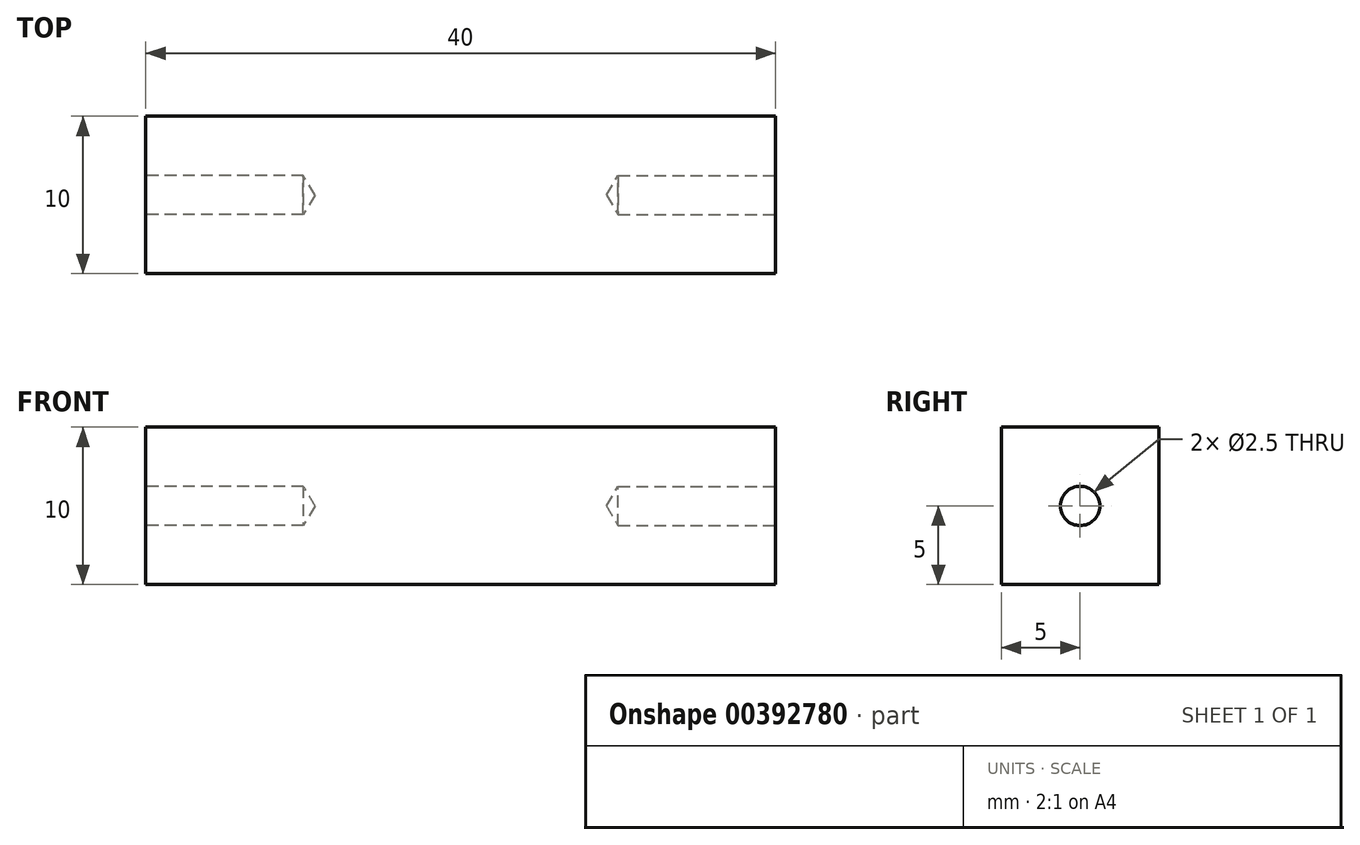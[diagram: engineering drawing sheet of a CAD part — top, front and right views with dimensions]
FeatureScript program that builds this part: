
annotation { "Feature Type Name" : "Feature", "Feature Type Description" : "" }
export const myFeature = defineFeature(function(context is Context, id is Id, definition is map)
    precondition{}
    {
        {
            var Q0;
            Q0=qCreatedBy(makeId("Right.planeOp"),FACE);
            var sketch = newSketch(context, id + "F0", { "sketchPlane" : qUnion([Q0])});
            skLineSegment(sketch, "E0.bottom", {"start": v(0, 0) * mm, "end": v(-10, 0) * mm});
            skLineSegment(sketch, "E0.top", {"start": v(0, 10) * mm, "end": v(-10, 10) * mm});
            skLineSegment(sketch, "E0.left", {"start": v(0, 0) * mm, "end": v(0, 10) * mm});
            skLineSegment(sketch, "E0.right", {"start": v(-10, 0) * mm, "end": v(-10, 10) * mm});
            skSolve(sketch);
        }
        {
            var Q0;
            Q0=makeQuery(id+"F0.imprint","IMPRINT",FACE,{"disambiguationData":[TD([[makeQuery(id+"F0.imprint","IMPRINT",EDGE,{"derivedFrom":sQuery(id+"F0.wireOp",EDGE,"E0.bottom")}),-1.0]])]});
            extrude(context, id + "F1", {"entities" : qUnion([Q0]), "depth" : 40 * mm});
        }
        {
            var Q0;
            Q0=makeQuery(id+"F1.opExtrude","CAP_FACE",FACE,{"disambiguationData":[OSD([sQuery(id+"F0.wireOp",EDGE,"E0.bottom"),sQuery(id+"F0.wireOp",EDGE,"E0.top"),sQuery(id+"F0.wireOp",EDGE,"E0.left"),sQuery(id+"F0.wireOp",EDGE,"E0.right")])],"isStart":false});
            var sketch = newSketch(context, id + "F2", { "sketchPlane" : qUnion([Q0])});
            skPoint(sketch, "E1.oppositeSnap0", {"position": v(0, 5) * mm});
            skLineSegment(sketch, "E1.bottom", {"start": v(0, 10) * mm, "end": v(-5, 10) * mm});
            skLineSegment(sketch, "E1.top", {"start": v(0, 5) * mm, "end": v(-5, 5) * mm});
            skLineSegment(sketch, "E1.left", {"start": v(0, 10) * mm, "end": v(0, 5) * mm});
            skLineSegment(sketch, "E1.right", {"start": v(-5, 10) * mm, "end": v(-5, 5) * mm});
            skSolve(sketch);
        }
        {
            var Q0;
            Q0=sQuery(id+"F2.wireOp",VERTEX,"E1.top.end");
            var Q1;
            Q1=makeQuery(id+"F1.opExtrude","SWEPT_BODY",BODY,{"disambiguationData":[OSD([sQuery(id+"F0.wireOp",EDGE,"E0.bottom"),sQuery(id+"F0.wireOp",EDGE,"E0.top"),sQuery(id+"F0.wireOp",EDGE,"E0.left"),sQuery(id+"F0.wireOp",EDGE,"E0.right")])]});
            hole(context, id + "F3", {"style" : HoleStyle.SIMPLE, "endStyle" : HoleEndStyle.BLIND, "holeDiameter" : 2.5 * mm, "holeDepth" : 10 * mm, "isTappedThrough" : true, "tappedDepth" : 12 * mm, "tapClearance" : 3, "locations" : qUnion([Q0]), "scope" : qUnion([Q1])});
        }
        {
            var Q0;
            Q0=makeQuery(id+"F1.opExtrude","CAP_FACE",FACE,{"disambiguationData":[OSD([sQuery(id+"F0.wireOp",EDGE,"E0.bottom"),sQuery(id+"F0.wireOp",EDGE,"E0.top"),sQuery(id+"F0.wireOp",EDGE,"E0.left"),sQuery(id+"F0.wireOp",EDGE,"E0.right")])],"isStart":true});
            var sketch = newSketch(context, id + "F4", { "sketchPlane" : qUnion([Q0])});
            skLineSegment(sketch, "E2.bottom", {"start": v(0, 10) * mm, "end": v(5, 10) * mm});
            skLineSegment(sketch, "E2.top", {"start": v(0, 5) * mm, "end": v(5, 5) * mm});
            skLineSegment(sketch, "E2.left", {"start": v(0, 10) * mm, "end": v(0, 5) * mm});
            skLineSegment(sketch, "E2.right", {"start": v(5, 10) * mm, "end": v(5, 5) * mm});
            skSolve(sketch);
        }
        {
            var Q0;
            Q0=sQuery(id+"F4.wireOp",VERTEX,"E2.right.end");
            var Q1;
            Q1=makeQuery(id+"F1.opExtrude","SWEPT_BODY",BODY,{"disambiguationData":[OSD([sQuery(id+"F0.wireOp",EDGE,"E0.bottom"),sQuery(id+"F0.wireOp",EDGE,"E0.top"),sQuery(id+"F0.wireOp",EDGE,"E0.left"),sQuery(id+"F0.wireOp",EDGE,"E0.right")])]});
            hole(context, id + "F5", {"style" : HoleStyle.SIMPLE, "endStyle" : HoleEndStyle.BLIND, "holeDiameter" : 2.5 * mm, "holeDepth" : 10 * mm, "isTappedThrough" : true, "tappedDepth" : 12 * mm, "tapClearance" : 3, "locations" : qUnion([Q0]), "scope" : qUnion([Q1])});
        }
    });
